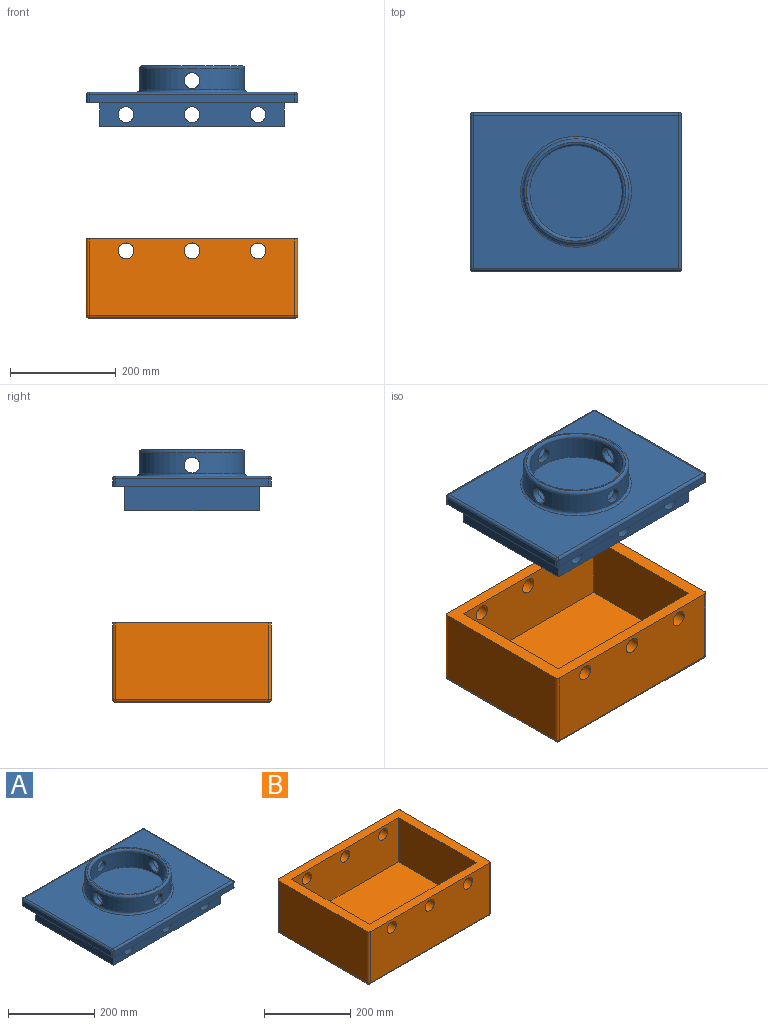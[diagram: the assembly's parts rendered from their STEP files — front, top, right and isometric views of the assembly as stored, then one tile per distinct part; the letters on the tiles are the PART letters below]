
ASSEMBLY  parts=2 mates=4
PART A: 37 faces, bbox 400x300x115 mm
  f0: plane 350x45mm, normal (0,-1,0), area 13629.4mm2, adj f1,f17,f18,f20,f21,f22,f23
  f1: plane 400x300mm, normal (0,0,-1), area 30728.5mm2, adj f0,f4,f5,f6,f7,f17,f18,f19
  f2: cylinder r=87.5mm len=175mm, axis (0,0,-1), area 21340.5mm2, adj f10,f11,f13,f14,f15,f16
  f3: cylinder r=100mm len=200mm, axis (0,0,-1), area 21656.1mm2, adj f12,f13,f14,f15,f16,f24
  f4: plane 290x15mm, normal (1,0,0), area 4350mm2, adj f1,f27,f33,f36
  f5: plane 390x15mm, normal (0,1,0), area 5850mm2, adj f1,f30,f34,f36
  f6: plane 290x15mm, normal (-1,0,0), area 4350mm2, adj f1,f25,f29,f30
  f7: plane 390x15mm, normal (0,-1,0), area 5850mm2, adj f1,f25,f27,f28
  f8: plane 390x290mm, normal (0,0,1), area 78463.9mm2, adj f24,f28,f29,f33,f34
  f9: plane 188x188mm, normal (0,0,1), area 294.5mm2, adj f11,f12
  f10: plane 175x175mm, normal (0,0,1), area 24052.8mm2, adj f2
  f11: torus R=93.5mm, axis (0,0,1), area 5310.7mm2, adj f2,f9
  f12: torus R=94mm, axis (0,0,1), area 5792.7mm2, adj f3,f9
  f13: cylinder r=15mm len=30mm, axis (0,-1,0), area 1185.8mm2, adj f2,f3
  f14: cylinder r=15mm len=30mm, axis (0,-1,0), area 1185.8mm2, adj f2,f3
  f15: cylinder r=15mm len=30mm, axis (-1,0,0), area 1185.8mm2, adj f2,f3
  f16: cylinder r=15mm len=30mm, axis (-1,0,0), area 1185.8mm2, adj f2,f3
  f17: plane 255x45mm, normal (1,0,0), area 11475mm2, adj f0,f1,f19,f20
  f18: plane 255x45mm, normal (-1,0,0), area 11475mm2, adj f0,f1,f19,f20
  f19: plane 350x45mm, normal (0,1,0), area 13629.4mm2, adj f1,f17,f18,f20,f21,f22,f23
  f20: plane 350x255mm, normal (0,0,-1), area 89250mm2, adj f0,f17,f18,f19
  f21: cylinder r=15mm len=255mm, axis (0,-1,0), area 24033.2mm2, adj f0,f19
  f22: cylinder r=15mm len=255mm, axis (0,-1,0), area 24033.2mm2, adj f0,f19
  f23: cylinder r=15mm len=255mm, axis (0,-1,0), area 24033.2mm2, adj f0,f19
  f24: torus R=105mm, axis (0,0,1), area 5024.5mm2, adj f3,f8
  f25: cylinder r=5mm len=15mm, axis (0,0,-1), area 117.8mm2, adj f1,f6,f7,f26
  f26: sphere r=5mm, area 39.3mm2, adj f25,f28,f29
  f27: cylinder r=5mm len=15mm, axis (0,0,1), area 117.8mm2, adj f1,f4,f7,f31
  f28: cylinder r=5mm len=390mm, axis (-1,0,0), area 3063.1mm2, adj f7,f8,f26,f31
  f29: cylinder r=5mm len=290mm, axis (0,1,0), area 2277.7mm2, adj f6,f8,f26,f32
  f30: cylinder r=5mm len=15mm, axis (0,0,1), area 117.8mm2, adj f1,f5,f6,f32
  f31: sphere r=5mm, area 39.3mm2, adj f27,f28,f33
  f32: sphere r=5mm, area 39.3mm2, adj f29,f30,f34
  f33: cylinder r=5mm len=290mm, axis (0,-1,0), area 2277.7mm2, adj f4,f8,f31,f35
  f34: cylinder r=5mm len=390mm, axis (1,0,0), area 3063.1mm2, adj f5,f8,f32,f35
  f35: sphere r=5mm, area 39.3mm2, adj f33,f34,f36
  f36: cylinder r=5mm len=15mm, axis (0,0,-1), area 117.8mm2, adj f1,f4,f5,f35
PART B: 29 faces, bbox 400x300x150 mm
  f0: plane 290x145mm, normal (-1,0,0), area 42050mm2, adj f4,f16,f20,f22
  f1: plane 390x145mm, normal (0,-1,0), area 54429.4mm2, adj f4,f13,f19,f22,f23,f24,f25
  f2: plane 290x145mm, normal (1,0,0), area 42050mm2, adj f4,f11,f13,f14
  f3: plane 390x145mm, normal (0,1,0), area 54429.4mm2, adj f4,f11,f15,f16,f26,f27,f28
  f4: plane 400x300mm, normal (0,0,1), area 30728.5mm2, adj f0,f1,f2,f3,f6,f7,f8,f9
  f5: plane 390x290mm, normal (0,0,-1), area 113100mm2, adj f14,f15,f19,f20
  f6: plane 255x125mm, normal (-1,0,0), area 31875mm2, adj f4,f7,f9,f10
  f7: plane 350x125mm, normal (0,-1,0), area 41629.4mm2, adj f4,f6,f8,f10,f26,f27,f28
  f8: plane 255x125mm, normal (1,0,0), area 31875mm2, adj f4,f7,f9,f10
  f9: plane 350x125mm, normal (0,1,0), area 41629.4mm2, adj f4,f6,f8,f10,f23,f24,f25
  f10: plane 350x255mm, normal (0,0,1), area 89250mm2, adj f6,f7,f8,f9
  f11: cylinder r=5mm len=145mm, axis (0,0,-1), area 1138.8mm2, adj f2,f3,f4,f12
  f12: sphere r=5mm, area 39.3mm2, adj f11,f14,f15
  f13: cylinder r=5mm len=145mm, axis (0,0,1), area 1138.8mm2, adj f1,f2,f4,f17
  f14: cylinder r=5mm len=290mm, axis (0,1,0), area 2277.7mm2, adj f2,f5,f12,f17
  f15: cylinder r=5mm len=390mm, axis (-1,0,0), area 3063.1mm2, adj f3,f5,f12,f18
  f16: cylinder r=5mm len=145mm, axis (0,0,1), area 1138.8mm2, adj f0,f3,f4,f18
  f17: sphere r=5mm, area 39.3mm2, adj f13,f14,f19
  f18: sphere r=5mm, area 39.3mm2, adj f15,f16,f20
  f19: cylinder r=5mm len=390mm, axis (1,0,0), area 3063.1mm2, adj f1,f5,f17,f21
  f20: cylinder r=5mm len=290mm, axis (0,-1,0), area 2277.7mm2, adj f0,f5,f18,f21
  f21: sphere r=5mm, area 39.3mm2, adj f19,f20,f22
  f22: cylinder r=5mm len=145mm, axis (0,0,-1), area 1138.8mm2, adj f0,f1,f4,f21
  f23: cylinder r=15mm len=30mm, axis (0,-1,0), area 2120.6mm2, adj f1,f9
  f24: cylinder r=15mm len=30mm, axis (0,-1,0), area 2120.6mm2, adj f1,f9
  f25: cylinder r=15mm len=30mm, axis (0,-1,0), area 2120.6mm2, adj f1,f9
  f26: cylinder r=15mm len=30mm, axis (0,-1,0), area 2120.6mm2, adj f3,f7
  f27: cylinder r=15mm len=30mm, axis (0,-1,0), area 2120.6mm2, adj f3,f7
  f28: cylinder r=15mm len=30mm, axis (0,-1,0), area 2120.6mm2, adj f3,f7
PLACE A t=(-51.76,-0.77,464.02)mm
PLACE B t=(-51.76,-0.77,56.02)mm
MATE parallel A.f2 <-> B.f4  axis (0,0,-1) through (-51.76,-0.77,464.02)mm
MATE parallel A.f22 <-> B.f23  axis (0,-1,0) through (-51.76,-128.27,441.52)mm
MATE parallel A.f22 <-> B.f25  axis (0,-1,0) through (-51.76,-128.27,441.52)mm
MATE parallel A.f2 <-> B.f4  axis (0,0,-1) through (-51.76,-0.77,464.02)mm
